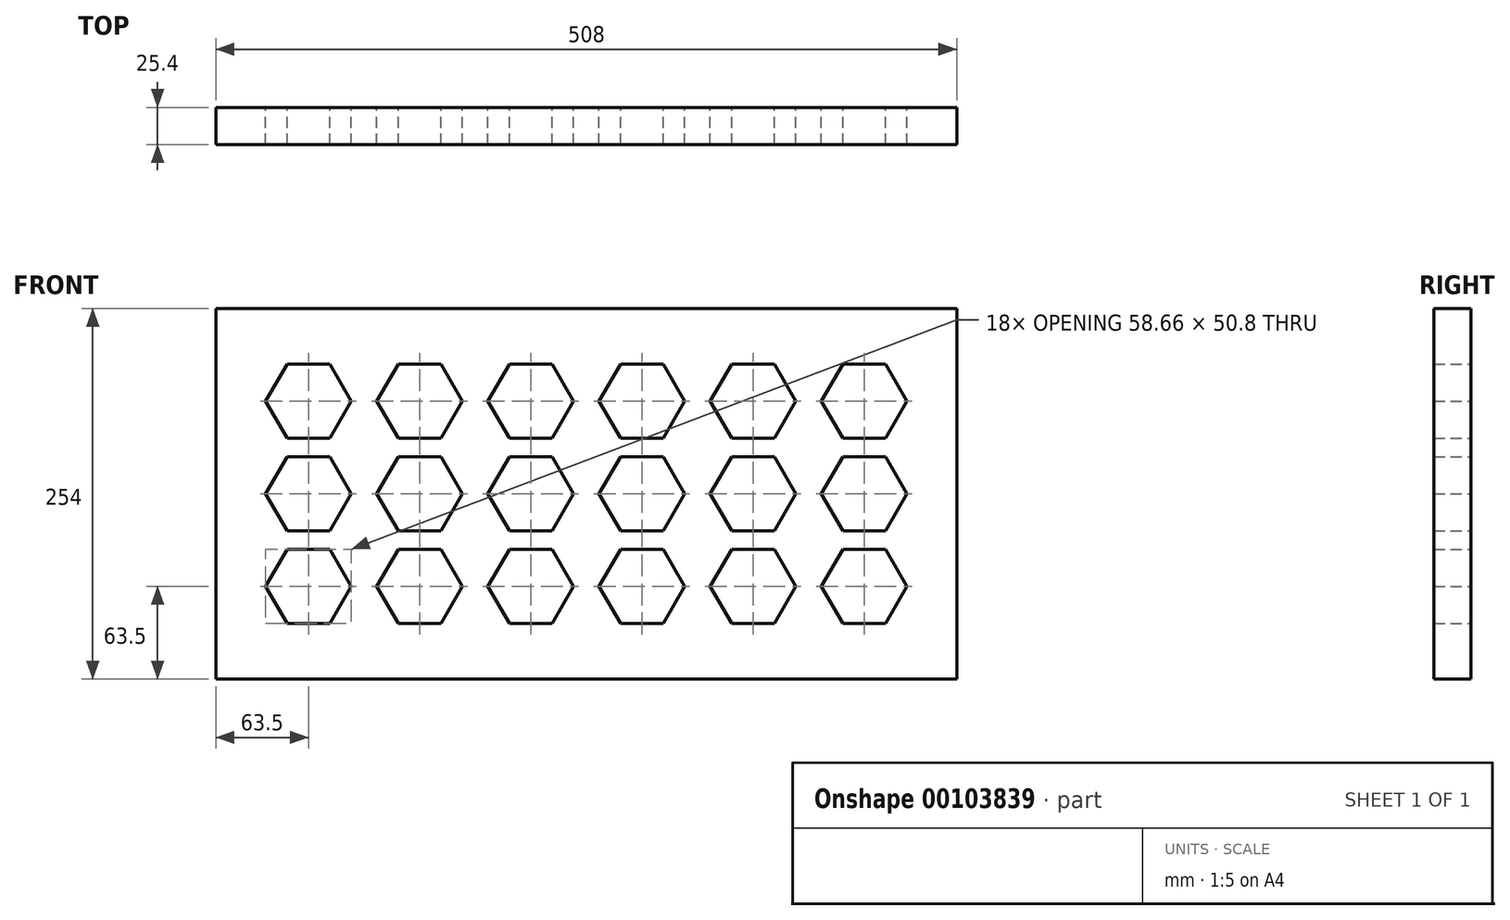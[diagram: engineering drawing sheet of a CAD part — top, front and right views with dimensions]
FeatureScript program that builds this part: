
annotation { "Feature Type Name" : "Feature", "Feature Type Description" : "" }
export const myFeature = defineFeature(function(context is Context, id is Id, definition is map)
    precondition{}
    {
        {
            var Q0;
            Q0=qCreatedBy(makeId("Front.planeOp"),FACE);
            var sketch = newSketch(context, id + "F0", { "sketchPlane" : qUnion([Q0])});
            skLineSegment(sketch, "E0.bottom", {"start": v(-254, 127) * mm, "end": v(254, 127) * mm});
            skLineSegment(sketch, "E0.top", {"start": v(-254, -127) * mm, "end": v(254, -127) * mm});
            skLineSegment(sketch, "E0.left", {"start": v(-254, 127) * mm, "end": v(-254, -127) * mm});
            skLineSegment(sketch, "E0.right", {"start": v(254, 127) * mm, "end": v(254, -127) * mm});
            skCircle(sketch, "E1.cCircle", {"center": v(-190.5, 63.5) * mm, "radius": 25.4 * mm, "construction": true});
            skLineSegment(sketch, "E1.0", {"start": v(-161.17, 63.5) * mm, "end": v(-175.84, 38.1) * mm});
            skLineSegment(sketch, "E1.1", {"start": v(-175.84, 38.1) * mm, "end": v(-205.16, 38.1) * mm});
            skLineSegment(sketch, "E1.2", {"start": v(-205.16, 38.1) * mm, "end": v(-219.83, 63.5) * mm});
            skLineSegment(sketch, "E1.3", {"start": v(-219.83, 63.5) * mm, "end": v(-205.16, 88.9) * mm});
            skLineSegment(sketch, "E1.4", {"start": v(-205.16, 88.9) * mm, "end": v(-175.84, 88.9) * mm});
            skLineSegment(sketch, "E1.5", {"start": v(-175.84, 88.9) * mm, "end": v(-161.17, 63.5) * mm});
            skPoint(sketch, "E1.0.midPoint", {"position": v(-168.5, 50.8) * mm});
            skLineSegment(sketch, "E2.1.0.0", {"start": v(-84.97, 63.5) * mm, "end": v(-99.64, 38.1) * mm});
            skPoint(sketch, "E2.1.0.1", {"position": v(-92.3, 50.8) * mm});
            skLineSegment(sketch, "E2.1.0.2", {"start": v(-128.96, 38.1) * mm, "end": v(-143.63, 63.5) * mm});
            skCircle(sketch, "E2.1.0.3", {"center": v(-114.3, 63.5) * mm, "radius": 25.4 * mm, "construction": true});
            skLineSegment(sketch, "E2.1.0.4", {"start": v(-99.64, 38.1) * mm, "end": v(-128.96, 38.1) * mm});
            skLineSegment(sketch, "E2.1.0.5", {"start": v(-143.63, 63.5) * mm, "end": v(-128.96, 88.9) * mm});
            skLineSegment(sketch, "E2.1.0.6", {"start": v(-128.96, 88.9) * mm, "end": v(-99.64, 88.9) * mm});
            skLineSegment(sketch, "E2.1.0.7", {"start": v(-99.64, 88.9) * mm, "end": v(-84.97, 63.5) * mm});
            skLineSegment(sketch, "E2.2.0.0", {"start": v(-8.77, 63.5) * mm, "end": v(-23.44, 38.1) * mm});
            skPoint(sketch, "E2.2.0.1", {"position": v(-16.1, 50.8) * mm});
            skLineSegment(sketch, "E2.2.0.2", {"start": v(-52.76, 38.1) * mm, "end": v(-67.43, 63.5) * mm});
            skCircle(sketch, "E2.2.0.3", {"center": v(-38.1, 63.5) * mm, "radius": 25.4 * mm, "construction": true});
            skLineSegment(sketch, "E2.2.0.4", {"start": v(-23.44, 38.1) * mm, "end": v(-52.76, 38.1) * mm});
            skLineSegment(sketch, "E2.2.0.5", {"start": v(-67.43, 63.5) * mm, "end": v(-52.76, 88.9) * mm});
            skLineSegment(sketch, "E2.2.0.6", {"start": v(-52.76, 88.9) * mm, "end": v(-23.44, 88.9) * mm});
            skLineSegment(sketch, "E2.2.0.7", {"start": v(-23.44, 88.9) * mm, "end": v(-8.77, 63.5) * mm});
            skLineSegment(sketch, "E2.direction1", {"start": v(-175.84, 38.1) * mm, "end": v(-99.64, 38.1) * mm, "construction": true});
            skLineSegment(sketch, "E3.0.3.0", {"start": v(67.43, 63.5) * mm, "end": v(52.76, 38.1) * mm});
            skPoint(sketch, "E3.3.3.0", {"position": v(60.1, 50.8) * mm});
            skLineSegment(sketch, "E3.4.3.0", {"start": v(23.44, 38.1) * mm, "end": v(8.77, 63.5) * mm});
            skCircle(sketch, "E3.7.3.0", {"center": v(38.1, 63.5) * mm, "radius": 25.4 * mm, "construction": true});
            skLineSegment(sketch, "E3.9.3.0", {"start": v(52.76, 38.1) * mm, "end": v(23.44, 38.1) * mm});
            skLineSegment(sketch, "E3.12.3.0", {"start": v(8.77, 63.5) * mm, "end": v(23.44, 88.9) * mm});
            skLineSegment(sketch, "E3.15.3.0", {"start": v(23.44, 88.9) * mm, "end": v(52.76, 88.9) * mm});
            skLineSegment(sketch, "E3.18.3.0", {"start": v(52.76, 88.9) * mm, "end": v(67.43, 63.5) * mm});
            skLineSegment(sketch, "E3.0.4.0", {"start": v(143.63, 63.5) * mm, "end": v(128.96, 38.1) * mm});
            skPoint(sketch, "E3.3.4.0", {"position": v(136.3, 50.8) * mm});
            skLineSegment(sketch, "E3.4.4.0", {"start": v(99.64, 38.1) * mm, "end": v(84.97, 63.5) * mm});
            skCircle(sketch, "E3.7.4.0", {"center": v(114.3, 63.5) * mm, "radius": 25.4 * mm, "construction": true});
            skLineSegment(sketch, "E3.9.4.0", {"start": v(128.96, 38.1) * mm, "end": v(99.64, 38.1) * mm});
            skLineSegment(sketch, "E3.12.4.0", {"start": v(84.97, 63.5) * mm, "end": v(99.64, 88.9) * mm});
            skLineSegment(sketch, "E3.15.4.0", {"start": v(99.64, 88.9) * mm, "end": v(128.96, 88.9) * mm});
            skLineSegment(sketch, "E3.18.4.0", {"start": v(128.96, 88.9) * mm, "end": v(143.63, 63.5) * mm});
            skLineSegment(sketch, "E3.0.5.0", {"start": v(219.83, 63.5) * mm, "end": v(205.16, 38.1) * mm});
            skPoint(sketch, "E3.3.5.0", {"position": v(212.5, 50.8) * mm});
            skLineSegment(sketch, "E3.4.5.0", {"start": v(175.84, 38.1) * mm, "end": v(161.17, 63.5) * mm});
            skCircle(sketch, "E3.7.5.0", {"center": v(190.5, 63.5) * mm, "radius": 25.4 * mm, "construction": true});
            skLineSegment(sketch, "E3.9.5.0", {"start": v(205.16, 38.1) * mm, "end": v(175.84, 38.1) * mm});
            skLineSegment(sketch, "E3.12.5.0", {"start": v(161.17, 63.5) * mm, "end": v(175.84, 88.9) * mm});
            skLineSegment(sketch, "E3.15.5.0", {"start": v(175.84, 88.9) * mm, "end": v(205.16, 88.9) * mm});
            skLineSegment(sketch, "E3.18.5.0", {"start": v(205.16, 88.9) * mm, "end": v(219.83, 63.5) * mm});
            skLineSegment(sketch, "E4.0.1.0", {"start": v(143.63, 0) * mm, "end": v(128.96, -25.4) * mm});
            skLineSegment(sketch, "E4.0.1.1", {"start": v(-175.84, -25.4) * mm, "end": v(-205.16, -25.4) * mm});
            skPoint(sketch, "E4.0.1.2", {"position": v(-16.1, -12.7) * mm});
            skLineSegment(sketch, "E4.0.1.3", {"start": v(175.84, -25.4) * mm, "end": v(161.17, 0) * mm});
            skLineSegment(sketch, "E4.0.1.4", {"start": v(-128.96, -25.4) * mm, "end": v(-143.63, 0) * mm});
            skLineSegment(sketch, "E4.0.1.5", {"start": v(-84.97, 0) * mm, "end": v(-99.64, -25.4) * mm});
            skLineSegment(sketch, "E4.0.1.6", {"start": v(-161.17, 0) * mm, "end": v(-175.84, -25.4) * mm});
            skCircle(sketch, "E4.0.1.7", {"center": v(190.5, 0) * mm, "radius": 25.4 * mm, "construction": true});
            skLineSegment(sketch, "E4.0.1.8", {"start": v(-205.16, -25.4) * mm, "end": v(-219.83, 0) * mm});
            skLineSegment(sketch, "E4.0.1.9", {"start": v(-175.84, 25.4) * mm, "end": v(-161.17, 0) * mm});
            skLineSegment(sketch, "E4.0.1.10", {"start": v(-205.16, 25.4) * mm, "end": v(-175.84, 25.4) * mm});
            skLineSegment(sketch, "E4.0.1.11", {"start": v(205.16, -25.4) * mm, "end": v(175.84, -25.4) * mm});
            skLineSegment(sketch, "E4.0.1.12", {"start": v(23.44, -25.4) * mm, "end": v(8.77, 0) * mm});
            skPoint(sketch, "E4.0.1.13", {"position": v(60.1, -12.7) * mm});
            skLineSegment(sketch, "E4.0.1.14", {"start": v(128.96, 25.4) * mm, "end": v(143.63, 0) * mm});
            skLineSegment(sketch, "E4.0.1.15", {"start": v(-52.76, 25.4) * mm, "end": v(-23.44, 25.4) * mm});
            skLineSegment(sketch, "E4.0.1.16", {"start": v(84.97, 0) * mm, "end": v(99.64, 25.4) * mm});
            skCircle(sketch, "E4.0.1.17", {"center": v(-38.1, 0) * mm, "radius": 25.4 * mm, "construction": true});
            skLineSegment(sketch, "E4.0.1.18", {"start": v(175.84, 25.4) * mm, "end": v(205.16, 25.4) * mm});
            skLineSegment(sketch, "E4.0.1.19", {"start": v(-23.44, -25.4) * mm, "end": v(-52.76, -25.4) * mm});
            skPoint(sketch, "E4.0.1.20", {"position": v(-168.5, -12.7) * mm});
            skLineSegment(sketch, "E4.0.1.21", {"start": v(-67.43, 0) * mm, "end": v(-52.76, 25.4) * mm});
            skLineSegment(sketch, "E4.0.1.22", {"start": v(67.43, 0) * mm, "end": v(52.76, -25.4) * mm});
            skLineSegment(sketch, "E4.0.1.23", {"start": v(128.96, -25.4) * mm, "end": v(99.64, -25.4) * mm});
            skLineSegment(sketch, "E4.0.1.24", {"start": v(52.76, -25.4) * mm, "end": v(23.44, -25.4) * mm});
            skLineSegment(sketch, "E4.0.1.25", {"start": v(-128.96, 25.4) * mm, "end": v(-99.64, 25.4) * mm});
            skPoint(sketch, "E4.0.1.26", {"position": v(-92.3, -12.7) * mm});
            skLineSegment(sketch, "E4.0.1.27", {"start": v(52.76, 25.4) * mm, "end": v(67.43, 0) * mm});
            skLineSegment(sketch, "E4.0.1.28", {"start": v(-219.83, 0) * mm, "end": v(-205.16, 25.4) * mm});
            skLineSegment(sketch, "E4.0.1.29", {"start": v(205.16, 25.4) * mm, "end": v(219.83, 0) * mm});
            skLineSegment(sketch, "E4.0.1.30", {"start": v(99.64, 25.4) * mm, "end": v(128.96, 25.4) * mm});
            skLineSegment(sketch, "E4.0.1.31", {"start": v(-52.76, -25.4) * mm, "end": v(-67.43, 0) * mm});
            skLineSegment(sketch, "E4.0.1.32", {"start": v(-8.77, 0) * mm, "end": v(-23.44, -25.4) * mm});
            skLineSegment(sketch, "E4.0.1.33", {"start": v(23.44, 25.4) * mm, "end": v(52.76, 25.4) * mm});
            skCircle(sketch, "E4.0.1.34", {"center": v(-190.5, 0) * mm, "radius": 25.4 * mm, "construction": true});
            skPoint(sketch, "E4.0.1.35", {"position": v(212.5, -12.7) * mm});
            skLineSegment(sketch, "E4.0.1.36", {"start": v(-99.64, 25.4) * mm, "end": v(-84.97, 0) * mm});
            skLineSegment(sketch, "E4.0.1.37", {"start": v(-175.84, -25.4) * mm, "end": v(-99.64, -25.4) * mm, "construction": true});
            skLineSegment(sketch, "E4.0.1.38", {"start": v(99.64, -25.4) * mm, "end": v(84.97, 0) * mm});
            skLineSegment(sketch, "E4.0.1.39", {"start": v(-143.63, 0) * mm, "end": v(-128.96, 25.4) * mm});
            skLineSegment(sketch, "E4.0.1.40", {"start": v(161.17, 0) * mm, "end": v(175.84, 25.4) * mm});
            skLineSegment(sketch, "E4.0.1.41", {"start": v(-99.64, -25.4) * mm, "end": v(-128.96, -25.4) * mm});
            skCircle(sketch, "E4.0.1.42", {"center": v(38.1, 0) * mm, "radius": 25.4 * mm, "construction": true});
            skLineSegment(sketch, "E4.0.1.43", {"start": v(8.77, 0) * mm, "end": v(23.44, 25.4) * mm});
            skCircle(sketch, "E4.0.1.44", {"center": v(-114.3, 0) * mm, "radius": 25.4 * mm, "construction": true});
            skLineSegment(sketch, "E4.0.1.45", {"start": v(219.83, 0) * mm, "end": v(205.16, -25.4) * mm});
            skLineSegment(sketch, "E4.0.1.46", {"start": v(-23.44, 25.4) * mm, "end": v(-8.77, 0) * mm});
            skCircle(sketch, "E4.0.1.47", {"center": v(114.3, 0) * mm, "radius": 25.4 * mm, "construction": true});
            skPoint(sketch, "E4.0.1.48", {"position": v(136.3, -12.7) * mm});
            skLineSegment(sketch, "E4.direction1", {"start": v(128.96, 38.1) * mm, "end": v(154.36, 38.1) * mm, "construction": true});
            skLineSegment(sketch, "E4.direction2", {"start": v(128.96, 38.1) * mm, "end": v(128.96, -25.4) * mm, "construction": true});
            skLineSegment(sketch, "E5.0.0.2", {"start": v(143.63, -63.5) * mm, "end": v(128.96, -88.9) * mm});
            skLineSegment(sketch, "E5.3.0.2", {"start": v(-175.84, -88.9) * mm, "end": v(-205.16, -88.9) * mm});
            skPoint(sketch, "E5.6.0.2", {"position": v(-16.1, -76.2) * mm});
            skLineSegment(sketch, "E5.7.0.2", {"start": v(175.84, -88.9) * mm, "end": v(161.17, -63.5) * mm});
            skLineSegment(sketch, "E5.10.0.2", {"start": v(-128.96, -88.9) * mm, "end": v(-143.63, -63.5) * mm});
            skLineSegment(sketch, "E5.13.0.2", {"start": v(-84.97, -63.5) * mm, "end": v(-99.64, -88.9) * mm});
            skLineSegment(sketch, "E5.16.0.2", {"start": v(-161.17, -63.5) * mm, "end": v(-175.84, -88.9) * mm});
            skCircle(sketch, "E5.19.0.2", {"center": v(190.5, -63.5) * mm, "radius": 25.4 * mm, "construction": true});
            skLineSegment(sketch, "E5.21.0.2", {"start": v(-205.16, -88.9) * mm, "end": v(-219.83, -63.5) * mm});
            skLineSegment(sketch, "E5.24.0.2", {"start": v(-175.84, -38.1) * mm, "end": v(-161.17, -63.5) * mm});
            skLineSegment(sketch, "E5.27.0.2", {"start": v(-205.16, -38.1) * mm, "end": v(-175.84, -38.1) * mm});
            skLineSegment(sketch, "E5.30.0.2", {"start": v(205.16, -88.9) * mm, "end": v(175.84, -88.9) * mm});
            skLineSegment(sketch, "E5.33.0.2", {"start": v(23.44, -88.9) * mm, "end": v(8.77, -63.5) * mm});
            skPoint(sketch, "E5.36.0.2", {"position": v(60.1, -76.2) * mm});
            skLineSegment(sketch, "E5.37.0.2", {"start": v(128.96, -38.1) * mm, "end": v(143.63, -63.5) * mm});
            skLineSegment(sketch, "E5.40.0.2", {"start": v(-52.76, -38.1) * mm, "end": v(-23.44, -38.1) * mm});
            skLineSegment(sketch, "E5.43.0.2", {"start": v(84.97, -63.5) * mm, "end": v(99.64, -38.1) * mm});
            skCircle(sketch, "E5.46.0.2", {"center": v(-38.1, -63.5) * mm, "radius": 25.4 * mm, "construction": true});
            skLineSegment(sketch, "E5.48.0.2", {"start": v(175.84, -38.1) * mm, "end": v(205.16, -38.1) * mm});
            skLineSegment(sketch, "E5.51.0.2", {"start": v(-23.44, -88.9) * mm, "end": v(-52.76, -88.9) * mm});
            skPoint(sketch, "E5.54.0.2", {"position": v(-168.5, -76.2) * mm});
            skLineSegment(sketch, "E5.55.0.2", {"start": v(-67.43, -63.5) * mm, "end": v(-52.76, -38.1) * mm});
            skLineSegment(sketch, "E5.58.0.2", {"start": v(67.43, -63.5) * mm, "end": v(52.76, -88.9) * mm});
            skLineSegment(sketch, "E5.61.0.2", {"start": v(128.96, -88.9) * mm, "end": v(99.64, -88.9) * mm});
            skLineSegment(sketch, "E5.64.0.2", {"start": v(52.76, -88.9) * mm, "end": v(23.44, -88.9) * mm});
            skLineSegment(sketch, "E5.67.0.2", {"start": v(-128.96, -38.1) * mm, "end": v(-99.64, -38.1) * mm});
            skPoint(sketch, "E5.70.0.2", {"position": v(-92.3, -76.2) * mm});
            skLineSegment(sketch, "E5.71.0.2", {"start": v(52.76, -38.1) * mm, "end": v(67.43, -63.5) * mm});
            skLineSegment(sketch, "E5.74.0.2", {"start": v(-219.83, -63.5) * mm, "end": v(-205.16, -38.1) * mm});
            skLineSegment(sketch, "E5.77.0.2", {"start": v(205.16, -38.1) * mm, "end": v(219.83, -63.5) * mm});
            skLineSegment(sketch, "E5.80.0.2", {"start": v(99.64, -38.1) * mm, "end": v(128.96, -38.1) * mm});
            skLineSegment(sketch, "E5.83.0.2", {"start": v(-52.76, -88.9) * mm, "end": v(-67.43, -63.5) * mm});
            skLineSegment(sketch, "E5.86.0.2", {"start": v(-8.77, -63.5) * mm, "end": v(-23.44, -88.9) * mm});
            skLineSegment(sketch, "E5.89.0.2", {"start": v(23.44, -38.1) * mm, "end": v(52.76, -38.1) * mm});
            skCircle(sketch, "E5.92.0.2", {"center": v(-190.5, -63.5) * mm, "radius": 25.4 * mm, "construction": true});
            skPoint(sketch, "E5.94.0.2", {"position": v(212.5, -76.2) * mm});
            skLineSegment(sketch, "E5.95.0.2", {"start": v(-99.64, -38.1) * mm, "end": v(-84.97, -63.5) * mm});
            skLineSegment(sketch, "E5.98.0.2", {"start": v(-175.84, -88.9) * mm, "end": v(-99.64, -88.9) * mm, "construction": true});
            skLineSegment(sketch, "E5.101.0.2", {"start": v(99.64, -88.9) * mm, "end": v(84.97, -63.5) * mm});
            skLineSegment(sketch, "E5.104.0.2", {"start": v(-143.63, -63.5) * mm, "end": v(-128.96, -38.1) * mm});
            skLineSegment(sketch, "E5.107.0.2", {"start": v(161.17, -63.5) * mm, "end": v(175.84, -38.1) * mm});
            skLineSegment(sketch, "E5.110.0.2", {"start": v(-99.64, -88.9) * mm, "end": v(-128.96, -88.9) * mm});
            skCircle(sketch, "E5.113.0.2", {"center": v(38.1, -63.5) * mm, "radius": 25.4 * mm, "construction": true});
            skLineSegment(sketch, "E5.115.0.2", {"start": v(8.77, -63.5) * mm, "end": v(23.44, -38.1) * mm});
            skCircle(sketch, "E5.118.0.2", {"center": v(-114.3, -63.5) * mm, "radius": 25.4 * mm, "construction": true});
            skLineSegment(sketch, "E5.120.0.2", {"start": v(219.83, -63.5) * mm, "end": v(205.16, -88.9) * mm});
            skLineSegment(sketch, "E5.123.0.2", {"start": v(-23.44, -38.1) * mm, "end": v(-8.77, -63.5) * mm});
            skCircle(sketch, "E5.126.0.2", {"center": v(114.3, -63.5) * mm, "radius": 25.4 * mm, "construction": true});
            skPoint(sketch, "E5.128.0.2", {"position": v(136.3, -76.2) * mm});
            skLineSegment(sketch, "E6", {"start": v(0, 0) * mm, "end": v(254, 0) * mm, "construction": true});
            skSolve(sketch);
        }
        {
            var Q0;
            Q0=makeQuery(id+"F0.imprint","IMPRINT",FACE,{"disambiguationData":[TD([[makeQuery(id+"F0.imprint","IMPRINT",EDGE,{"derivedFrom":sQuery(id+"F0.wireOp",EDGE,"E0.bottom")}),-1.0]])]});
            extrude(context, id + "F1", {"entities" : qUnion([Q0]), "depth" : 25.4 * mm});
        }
    });
